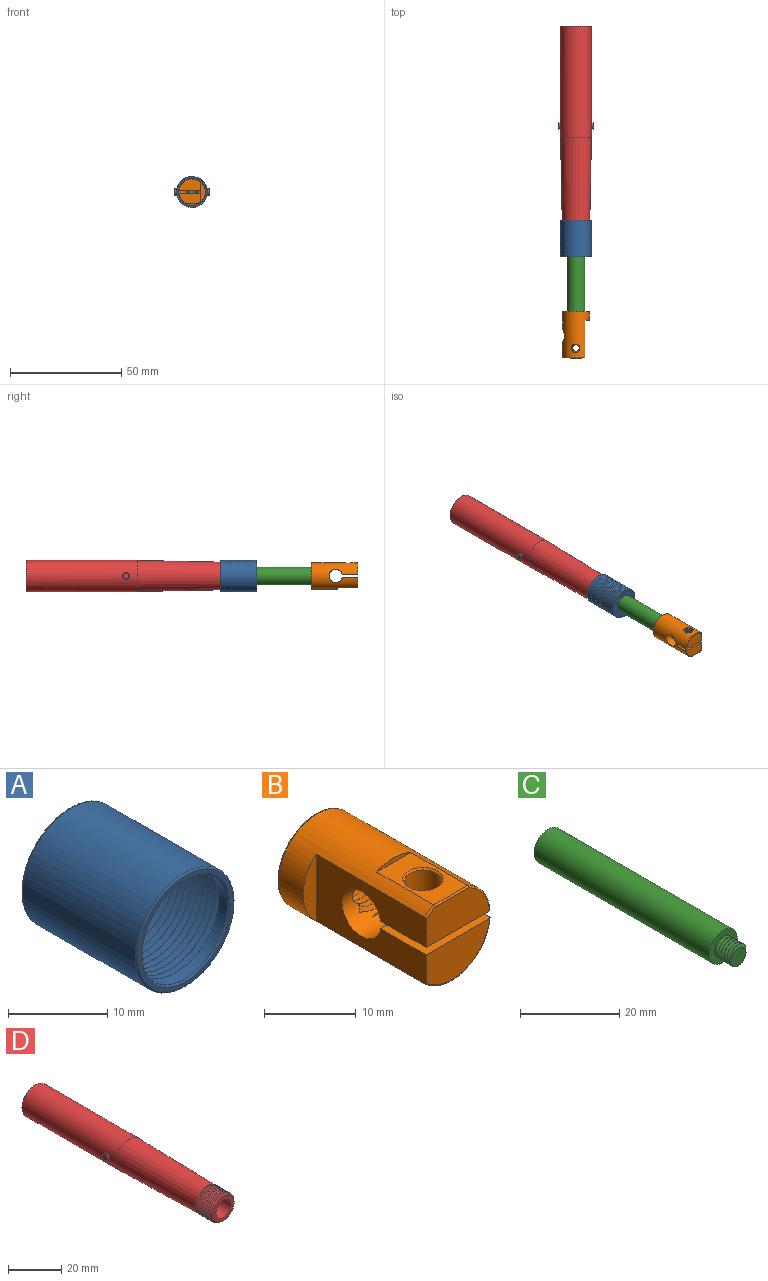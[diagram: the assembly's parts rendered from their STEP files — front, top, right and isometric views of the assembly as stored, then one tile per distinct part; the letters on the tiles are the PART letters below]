
ASSEMBLY  parts=4 mates=3
PART A: 29 faces, bbox 15.7x16.5x15.2 mm
  f0: cylinder r=6.12mm len=12.25mm, axis (0,1,0), area 54.6mm2, adj f1,f22,f24,f27
  f1: cylinder r=6.12mm len=12.25mm, axis (0,1,0), area 0.8mm2, adj f0,f2,f20,f24
  f2: cylinder r=6.12mm len=12.25mm, axis (0,1,0), area 0.8mm2, adj f1,f3,f20,f24
  f3: cylinder r=6.12mm len=12.25mm, axis (0,1,0), area 0.8mm2, adj f2,f4,f20,f24
  f4: cylinder r=6.12mm len=12.25mm, axis (0,1,0), area 0.8mm2, adj f3,f5,f20,f24
  f5: cylinder r=6.12mm len=12.25mm, axis (0,1,0), area 0.8mm2, adj f4,f6,f20,f24
  f6: cylinder r=6.12mm len=12.25mm, axis (0,1,0), area 0.8mm2, adj f5,f7,f20,f24
  f7: cylinder r=6.12mm len=12.25mm, axis (0,1,0), area 0.8mm2, adj f6,f8,f20,f24
  f8: cylinder r=6.12mm len=12.25mm, axis (0,1,0), area 0.8mm2, adj f7,f9,f20,f24
  f9: cylinder r=6.12mm len=12.25mm, axis (0,1,0), area 0.8mm2, adj f8,f10,f20,f24
  f10: cylinder r=6.12mm len=12.25mm, axis (0,1,0), area 0.8mm2, adj f9,f11,f20,f24
  f11: cylinder r=6.12mm len=12.25mm, axis (0,1,0), area 0.8mm2, adj f10,f12,f20,f24
  f12: cylinder r=6.12mm len=12.25mm, axis (0,1,0), area 0.8mm2, adj f11,f13,f20,f24
  f13: cylinder r=6.12mm len=12.25mm, axis (0,1,0), area 0.8mm2, adj f12,f14,f20,f24
  f14: cylinder r=6.12mm len=4.29mm, axis (0,1,0), area 0.1mm2, adj f13,f19,f20,f24
  f15: plane 13.6x13.6mm, normal (0,1,0), area 89.9mm2, adj f20,f21,f25,f26
  f16: cylinder r=7mm len=16.1mm, axis (0,1,0), area 708.1mm2, adj f26,f28
  f17: plane 13.6x13.6mm, normal (0,-1,0), area 19.6mm2, adj f27,f28
  f18: cylinder r=4mm len=8mm, axis (0,1,0), area 95.5mm2, adj f19,f25
  f19: plane 12.25x12.25mm, normal (0,-1,0), area 67.6mm2, adj f14,f18,f21
  f20: bspline ~15.71x14.92mm, area 573.5mm2, adj f1,f2,f3,f4,f5,f6,f7,f8
  f21: cylinder r=6.12mm len=12.25mm, axis (0,1,0), area 134.4mm2, adj f15,f19,f20,f23,f24
  f22: plane 0.78x0.68mm, normal (1,0,0), area 0.3mm2, adj f0,f20,f24
  f23: plane 0.78x0.48mm, normal (-0.71,0,0.71), area 0.3mm2, adj f20,f21,f24
  f24: bspline ~15.71x14.92mm, area 574.2mm2, adj f0,f1,f2,f3,f4,f5,f6,f7
  f25: torus R=4.2mm, axis (0,-1,0), area 8mm2, adj f15,f18
  f26: torus R=6.8mm, axis (0,-1,0), area 13.7mm2, adj f15,f16
  f27: torus R=6.33mm, axis (0,-1,0), area 12.2mm2, adj f0,f17
  f28: torus R=6.8mm, axis (0,-1,0), area 13.7mm2, adj f16,f17
PART B: 41 faces, bbox 13.4x21.4x13.4 mm
  f0: plane 10.42x7.49mm, normal (0,0,1), area 59.4mm2, adj f1,f3,f6,f7,f8,f19,f38,f39
  f1: bspline ~6.18x5.08mm, area 63.9mm2, adj f0,f2,f3,f7,f38
  f2: bspline ~3.81x1.4mm, area 0mm2, adj f1,f38
  f3: bspline ~5.83x5.08mm, area 62.3mm2, adj f0,f1,f4,f6,f7,f38
  f4: cylinder r=1.6mm len=1.16mm, axis (0,0,-1), area 0mm2, adj f3,f5,f38
  f5: bspline ~0.89x0.27mm, area 0mm2, adj f4,f38
  f6: plane 0.3x0.19mm, normal (-0.9,-0.43,0), area 0mm2, adj f0,f3,f7
  f7: cylinder r=1.6mm len=5.3mm, axis (0,0,-1), area -7.8mm2, adj f0,f1,f3,f6,f38
  f8: plane 17.07x9.01mm, normal (-1,0,0), area 116.7mm2, adj f0,f9,f16,f17,f18,f19,f38,f39
  f9: plane 9.99x7.05mm, normal (0,0,-1), area 57.7mm2, adj f8,f10,f15,f18,f19,f38
  f10: torus R=5.8mm, axis (0,-1,0), area 1.9mm2, adj f9,f11,f18,f38
  f11: cylinder r=0.2mm len=5.23mm, axis (1,0,0), area 1.6mm2, adj f10,f12,f17,f18
  f12: plane 8.8x5.23mm, normal (0,0,1), area 30.8mm2, adj f11,f13,f14,f38
  f13: plane 5.23x0.6mm, normal (0,-1,0), area 2.1mm2, adj f12,f38
  f14: cone r=2mm half-angle=45deg, axis (0,0,1), area 3.7mm2, adj f12,f15
  f15: cylinder r=2mm len=4.7mm, axis (0,0,1), area 59.1mm2, adj f9,f14
  f16: plane 8.94x2mm, normal (0,-1,0), area 12.4mm2, adj f8,f38
  f17: torus R=5.8mm, axis (0,-1,0), area 0.5mm2, adj f8,f11,f18,f38
  f18: plane 9.78x4.7mm, normal (0,-1,0), area 40.6mm2, adj f8,f9,f10,f11,f17
  f19: cylinder r=3mm len=10mm, axis (-1,0,0), area 150mm2, adj f0,f8,f9,f20,f27,f28,f29,f30
  f20: cylinder r=2.1mm len=5.14mm, axis (0,1,0), area 5mm2, adj f19,f21,f22,f31,f32
  f21: plane 0.78x0.68mm, normal (0,0,1), area 0.3mm2, adj f20,f31,f32
  f22: plane 8x8mm, normal (0,1,0), area 36.4mm2, adj f20,f23
  f23: cylinder r=4mm len=8mm, axis (0,1,0), area 62.8mm2, adj f22,f24
  f24: cone r=4mm half-angle=45deg, axis (0,1,0), area 18.9mm2, adj f23,f25
  f25: plane 11.6x11.6mm, normal (0,1,0), area 42.1mm2, adj f24,f26
  f26: torus R=5.8mm, axis (0,-1,0), area 11.7mm2, adj f25,f38
  f27: bspline ~4.81x1.73mm, area 0mm2, adj f19,f28
  f28: bspline ~4.81x1.73mm, area 1.5mm2, adj f19,f27,f29
  f29: cylinder r=2.1mm len=1.2mm, axis (0,1,0), area 0mm2, adj f19,f28,f30
  f30: bspline ~5.61x4.16mm, area 2.6mm2, adj f19,f29,f31
  f31: bspline ~5.55x5.55mm, area 76.7mm2, adj f19,f20,f21,f30,f32
  f32: bspline ~6.41x5.55mm, area 70.7mm2, adj f19,f20,f21,f31,f33
  f33: cylinder r=2.1mm len=3.06mm, axis (0,1,0), area 0.1mm2, adj f19,f32,f35
  f34: bspline ~4.81x1.73mm, area 0mm2, adj f19,f35
  f35: bspline ~4.81x1.73mm, area 3mm2, adj f19,f33,f34
  f36: bspline ~1.67x0.15mm, area 0mm2, adj f19,f37
  f37: bspline ~1.67x0.15mm, area 0mm2, adj f19,f36
  f38: cylinder r=6mm len=20.6mm, axis (0,1,0), area 512.1mm2, adj f0,f1,f2,f3,f4,f5,f7,f8
  f39: torus R=5.8mm, axis (0,-1,0), area 4.2mm2, adj f0,f8,f38,f40
  f40: plane 9.78x5.3mm, normal (0,-1,0), area 42.7mm2, adj f0,f8,f39
PART C: 8 faces, bbox 8.6x55.5x8.6 mm
  f0: cylinder r=2.5mm len=5mm, axis (0,1,0), area 7.2mm2, adj f2,f4,f5,f6,f7
  f1: cylinder r=4mm len=50mm, axis (0,1,0), area 1256.6mm2, adj f2,f3
  f2: plane 8x8mm, normal (0,-1,0), area 30.6mm2, adj f0,f1
  f3: plane 8x8mm, normal (0,1,0), area 50.3mm2, adj f1
  f4: plane 4.92x4.92mm, normal (0,-1,0), area 14.8mm2, adj f0,f6,f7
  f5: plane 0.79x0.68mm, normal (0,0,1), area 0.3mm2, adj f0,f6,f7
  f6: bspline ~5.77x5mm, area 52.2mm2, adj f0,f4,f5,f7
  f7: bspline ~5.77x5.06mm, area 57.8mm2, adj f0,f4,f5,f6
PART D: 22 faces, bbox 16x100x15.2 mm
  f0: cylinder r=5.6mm len=11.2mm, axis (0,-1,0), area 34.8mm2, adj f8,f11,f12,f14,f15
  f1: cone r=6mm half-angle=1.1deg, axis (0,1,0), area 1715mm2, adj f2,f8,f13,f14,f15
  f2: cylinder r=7mm len=49.8mm, axis (0,1,0), area 2176.1mm2, adj f1,f5,f6,f18
  f3: plane 13.6x13.6mm, normal (0,1,0), area 145.3mm2, adj f18
  f4: plane 2.6x2.6mm, normal (-1,0,0), area 5.3mm2, adj f16
  f5: cylinder r=1.5mm len=3mm, axis (-1,0,0), area 9.1mm2, adj f2,f16
  f6: cylinder r=1.5mm len=3mm, axis (-1,0,0), area 9.1mm2, adj f2,f17
  f7: plane 2.6x2.6mm, normal (1,0,0), area 5.3mm2, adj f17
  f8: plane 12.34x12.34mm, normal (0,-1,0), area 9.1mm2, adj f0,f1,f14,f15
  f9: plane 8x8mm, normal (0,-1,0), area 50.3mm2, adj f10
  f10: cylinder r=4mm len=50mm, axis (0,-1,0), area 1256.6mm2, adj f9,f11
  f11: plane 11.2x11.2mm, normal (0,-1,0), area 48.3mm2, adj f0,f10
  f12: plane 0.79x0.68mm, normal (0,0,-1), area 0.3mm2, adj f0,f14,f15
  f13: plane 0.13x0.08mm, normal (-0.71,0,-0.71), area 0mm2, adj f1,f14,f15
  f14: bspline ~14.51x12.57mm, area 308.2mm2, adj f0,f1,f8,f12,f13,f15
  f15: bspline ~14.51x12.57mm, area 294.3mm2, adj f0,f1,f8,f12,f13,f14
  f16: torus R=1.3mm, axis (1,0,0), area 2.8mm2, adj f4,f5
  f17: torus R=1.3mm, axis (1,0,0), area 2.8mm2, adj f6,f7
  f18: torus R=6.8mm, axis (0,1,0), area 13.7mm2, adj f2,f3
  f19: plane 11x11mm, normal (0,1,0), area 95mm2, adj f20
  f20: cylinder r=5.5mm len=30mm, axis (0,1,0), area 1036.7mm2, adj f19,f21
  f21: plane 11x11mm, normal (0,-1,0), area 95mm2, adj f20
PLACE A rot(axis=(0,0,1),180deg) t=(-33.32,-20.64,31.99)mm
PLACE B rot(axis=(0,-1,0),180deg) t=(-33.32,-45.14,31.99)mm
PLACE C rot(axis=(0,1,0),180deg) t=(-33.32,1.86,31.99)mm
PLACE D rot(axis=(0,1,0),180deg) t=(-33.32,83.36,31.99)mm
MATE fastened D.f0 <-> A.f0  axis (0,-1,0) through (-33.32,-16.64,31.99)mm
MATE cylindrical C.f0 <-> A.f0  axis (0,1,0) through (-33.32,1.86,31.99)mm
MATE fastened C.f0 <-> B.f10  axis (0,1,0) through (-33.32,-48.14,31.99)mm
